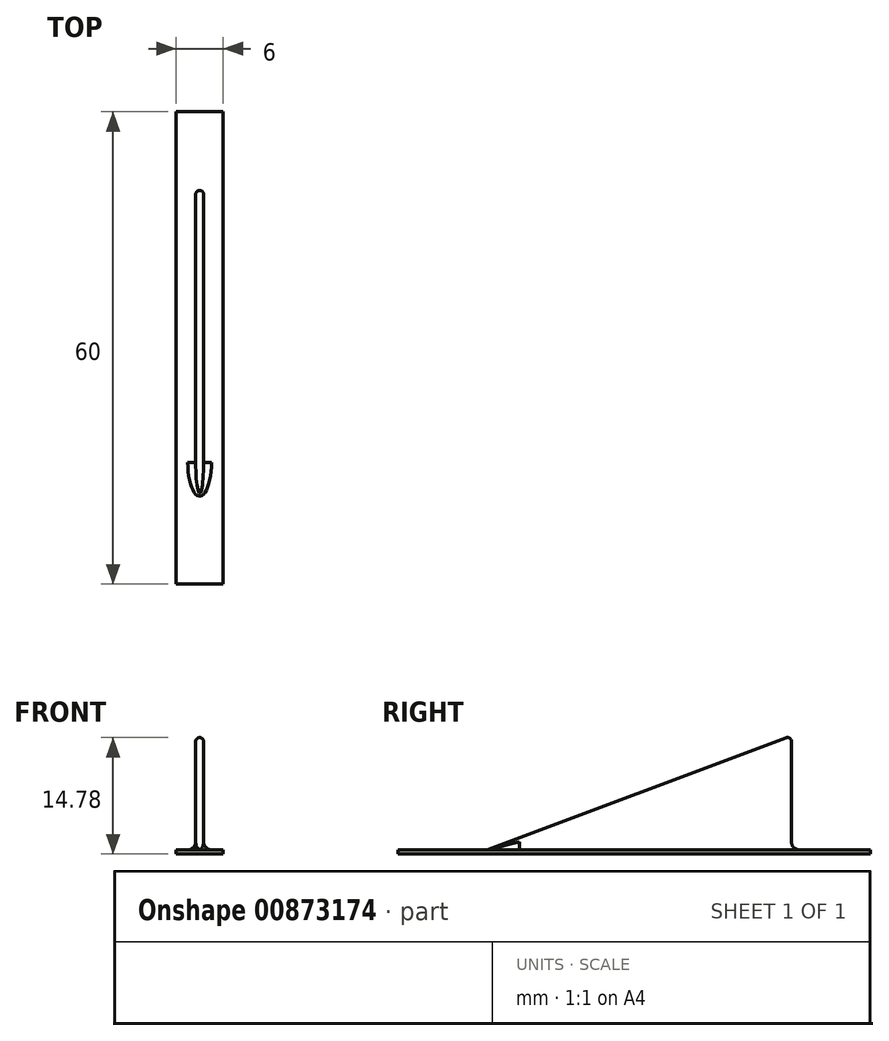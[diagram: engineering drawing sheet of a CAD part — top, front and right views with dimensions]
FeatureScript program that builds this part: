
annotation { "Feature Type Name" : "Feature", "Feature Type Description" : "" }
export const myFeature = defineFeature(function(context is Context, id is Id, definition is map)
    precondition{}
    {
        {
            var Q0;
            Q0=qCreatedBy(makeId("Top.planeOp"),FACE);
            var sketch = newSketch(context, id + "F0", { "sketchPlane" : qUnion([Q0])});
            skLineSegment(sketch, "E0.bottom", {"start": v(-3, 30) * mm, "end": v(3, 30) * mm});
            skLineSegment(sketch, "E0.top", {"start": v(-3, -30) * mm, "end": v(3, -30) * mm});
            skLineSegment(sketch, "E0.left", {"start": v(-3, 30) * mm, "end": v(-3, -30) * mm});
            skLineSegment(sketch, "E0.right", {"start": v(3, 30) * mm, "end": v(3, -30) * mm});
            skPoint(sketch, "E0.middle", {"position": v(0, 0) * mm});
            skSolve(sketch);
        }
        {
            var Q0;
            Q0=qSketchRegion(id+"F0",true);
            extrude(context, id + "F1", {"entities" : qUnion([Q0]), "depth" : 0.5 * mm, "offsetDistance" : 25 * mm});
        }
        {
            var Q0;
            Q0=qCreatedBy(makeId("Right.planeOp"),FACE);
            var sketch = newSketch(context, id + "F2", { "sketchPlane" : qUnion([Q0])});
            skLineSegment(sketch, "E1.0", {"start": v(20, 0) * mm, "end": v(-20, 0) * mm});
            skLineSegment(sketch, "E2", {"start": v(20, 0) * mm, "end": v(20, 15) * mm});
            skLineSegment(sketch, "E3", {"start": v(20, 15) * mm, "end": v(-20, 0) * mm});
            skSolve(sketch);
        }
        {
            var Q0;
            Q0=qSketchRegion(id+"F2",true);
            extrude(context, id + "F3", {"entities" : qUnion([Q0]), "operationType" : NewBodyOperationType.ADD, "depth" : 1 * mm, "offsetDistance" : 25 * mm, "symmetric" : true});
        }
        {
            var Q0;
            Q0=makeQuery(id+"F3.opExtrude","CAP_EDGE",EDGE,{"disambiguationData":[OSD([sQuery(id+"F2.wireOp",EDGE,"E3")])],"isStart":true});
            var Q1;
            Q1=makeQuery(id+"F3.opExtrude","CAP_EDGE",EDGE,{"disambiguationData":[OSD([sQuery(id+"F2.wireOp",EDGE,"E3")])],"isStart":false});
            var Q2;
            Q2=makeQuery(id+"F3.opExtrude","CAP_EDGE",EDGE,{"disambiguationData":[OSD([sQuery(id+"F2.wireOp",EDGE,"E2")])],"isStart":true});
            var Q3;
            Q3=makeQuery(id+"F3.opExtrude","CAP_EDGE",EDGE,{"disambiguationData":[OSD([sQuery(id+"F2.wireOp",EDGE,"E2")])],"isStart":false});
            var Q4;
            Q4=makeQuery(id+"F3.opExtrude","SWEPT_EDGE",EDGE,{"disambiguationData":[OSD([sQuery(id+"F2.wireOp",EDGE,"E2"),sQuery(id+"F2.wireOp",EDGE,"E3")])]});
            fillet(context, id + "F4", {"entities" : qUnion([Q0, Q1, Q2, Q3, Q4]), "radius" : 0.5 * mm, "allowEdgeOverflow" : false});
        }
        {
            var Q0;
            Q0=makeQuery(id+"F3.boolean.opBoolean","INTERSECT",EDGE,{"derivedFrom":[makeQuery(id+"F1.opExtrude","CAP_FACE",FACE,{"disambiguationData":[OSD([sQuery(id+"F0.wireOp",EDGE,"E0.bottom"),sQuery(id+"F0.wireOp",EDGE,"E0.top"),sQuery(id+"F0.wireOp",EDGE,"E0.left"),sQuery(id+"F0.wireOp",EDGE,"E0.right")])],"isStart":false}),makeQuery(id+"F3.opExtrude","CAP_FACE",FACE,{"disambiguationData":[OSD([sQuery(id+"F2.wireOp",EDGE,"E1.0"),sQuery(id+"F2.wireOp",EDGE,"E2"),sQuery(id+"F2.wireOp",EDGE,"E3")])],"isStart":true})]});
            fillet(context, id + "F5", {"entities" : qUnion([Q0]), "radius" : 1 * mm, "tangentPropagation" : true, "allowEdgeOverflow" : false});
        }
    });
